# Revit family: КШ РАШВОРК  арт.7025 .rfa
name_source: partatom
category: Арматура трубопроводов
units: mm (PartAtom-declared; Revit-internal decimal feet)

## family parameters
Всегда вертикально = Нет
На основе рабочей плоскости = Нет
Общий = Нет
При загрузке вырезать с полостями = Да
Размер круглого соединителя = Использовать диаметр
Тип детали = Нормальный

## types (11) — shared parameters
ADSK_Единица измерения = шт
ADSK_Завод-изготовитель = ООО "ТД "РАШВОРК"
URL = https://rwru.ru
Изготовитель = ООО "ТД "РАШВОРК"
Корпус = нерж. сталь CF8M
Ручка = нерж. сталь AISI304
Уго_длинна = 115 мм
zero-valued in all types: Отметка по умолчанию

## per-type parameters (varying)
| type | ADSK_Код изделия | ADSK_Масса | DN | DN_соединителя | H | H1 | H11 | H2 | H3 | L | L1 | L2 | L3 | L4 | LL | Lруч | TISO | W | Корпус_ | РАСС | ШISO | Шручки |
| Кран шаровой полнопроходной РАШВОРК 7025 DN008 PN63, CF8M / AISI316 / PTFE, ВР/ВР, ISO 5211, рукоятка-рычаг, кв.9мм | 7025-008-63 | 0.4 | 13 мм | 8 мм | 60 мм | 30 мм | 13 мм | 1 мм | 8 мм | 52 мм | 35 мм | 10 мм | 10 мм | 14 мм | 20 мм | 100 мм | 4 мм | 140 мм | Корпус_ : DN8_10 | 33 мм | 32 мм | 20 мм |
| Кран шаровой полнопроходной РАШВОРК 7025 DN100 PN63, CF8M / AISI316 / PTFE, ВР/ВР, ISO 5211, рукоятка-рычаг, кв.17мм | 7025-100-63 | 14.37 | 94 мм | 100 мм | 182 мм | 131 мм | 76 мм | 8 мм | 15 мм | 213 мм | 152 мм | 33 мм | 27 мм | 29 мм | 115 мм | 245 мм | 10 мм | 320 мм | Корпус_ : DN100 | 152 мм | 102 мм | 32 мм |
| Кран шаровой полнопроходной РАШВОРК 7025 DN010 PN63, CF8M / AISI316 / PTFE, ВР/ВР, ISO 5211, рукоятка-рычаг, кв.9мм | 7025-010-63 | 0.42 | 13 мм | 10 мм | 60 мм | 30 мм | 13 мм | 1 мм | 8 мм | 52 мм | 35 мм | 10 мм | 10 мм | 14 мм | 20 мм | 100 мм | 4 мм | 140 мм | Корпус_ : DN8_10 | 33 мм | 32 мм | 20 мм |
| Кран шаровой полнопроходной РАШВОРК 7025 DN015 PN63, CF8M / AISI316 / PTFE, ВР/ВР, ISO 5211, рукоятка-рычаг, кв.9мм | 7025-015-63 | 0.53 | 15 мм | 15 мм | 68 мм | 37 мм | 16 мм | 1 мм | 10 мм | 62 мм | 38 мм | 10 мм | 10 мм | 16 мм | 25 мм | 100 мм | 5 мм | 140 мм | Корпус_ : DN15 | 38 мм | 42 мм | 20 мм |
| Кран шаровой полнопроходной РАШВОРК 7025 DN020 PN63, CF8M / AISI316 / PTFE, ВР/ВР, ISO 5211, рукоятка-рычаг, кв.9мм | 7025-020-63 | 0.68 | 20 мм | 20 мм | 72 мм | 41 мм | 20 мм | 1 мм | 6 мм | 72 мм | 48 мм | 14 мм | 10 мм | 16 мм | 31 мм | 100 мм | 5 мм | 140 мм | Корпус_ : DN20 | 48 мм | 42 мм | 20 мм |
| Кран шаровой полнопроходной РАШВОРК 7025 DN025 PN63, CF8M / AISI316 / PTFE, ВР/ВР, ISO 5211, рукоятка-рычаг, кв.11мм | 7025-025-63 | 0.97 | 25 мм | 25 мм | 86 мм | 49 мм | 25 мм | 2 мм | 11 мм | 72 мм | 51 мм | 16 мм | 10 мм | 18 мм | 39 мм | 90 мм | 6 мм | 160 мм | Корпус_ : DN25 | 51 мм | 50 мм | 22 мм |
| Кран шаровой полнопроходной РАШВОРК 7025 DN032 PN63, CF8M / AISI316 / PTFE, ВР/ВР, ISO 5211, рукоятка-рычаг, кв.11мм | 7025-032-63 | 1.55 | 32 мм | 32 мм | 94 мм | 53 мм | 30 мм | 2 мм | 11 мм | 72 мм | 55 мм | 15 мм | 10 мм | 18 мм | 48 мм | 90 мм | 6 мм | 160 мм | Корпус_ : DN32 | 64 мм | 50 мм | 22 мм |
| Кран шаровой полнопроходной РАШВОРК 7025 DN040 PN63, CF8M / AISI316 / PTFE, ВР/ВР, ISO 5211, рукоятка-рычаг, кв.14мм | 7025-040-63 | 2.18 | 38 мм | 40 мм | 101 мм | 62 мм | 34 мм | 2 мм | 16 мм | 103 мм | 71 мм | 18 мм | 16 мм | 23 мм | 54 мм | 130 мм | 6 мм | 185 мм | Корпус_ : DN40 | 71 мм | 70 мм | 25 мм |
| Кран шаровой полнопроходной РАШВОРК 7025 DN050 PN63, CF8M / AISI316 / PTFE, ВР/ВР, ISO 5211, рукоятка-рычаг, кв.14мм | 7025-050-63 | 3.19 | 50 мм | 50 мм | 110 мм | 71 мм | 44 мм | 2 мм | 16 мм | 126 мм | 90 мм | 20 мм | 16 мм | 23 мм | 68 мм | 130 мм | 6 мм | 185 мм | Корпус_ : DN50 | 90 мм | 70 мм | 25 мм |
| Кран шаровой полнопроходной РАШВОРК 7025 DN065 PN63, CF8M / AISI316 / PTFE, ВР/ВР, ISO 5211, рукоятка-рычаг, кв.17мм | 7025-065-63 | 6.22 | 65 мм | 65 мм | 143 мм | 96 мм | 55 мм | 2 мм | 16 мм | 158 мм | 112 мм | 25 мм | 20 мм | 30 мм | 85 мм | 155 мм | 10 мм | 230 мм | Корпус_ : DN65 | 112 мм | 102 мм | 25 мм |
| Кран шаровой полнопроходной РАШВОРК 7025 DN080 PN63, CF8M / AISI316 / PTFE, ВР/ВР, ISO 5211, рукоятка-рычаг, кв.17мм | 7025-080-63 | 8.3 | 76 мм | 80 мм | 157 мм | 109 мм | 62 мм | 3 мм | 16 мм | 179 мм | 128 мм | 28 мм | 20 мм | 30 мм | 96 мм | 155 мм | 10 мм | 230 мм | Корпус_ : DN80 | 128 мм | 102 мм | 32 мм |

note: column(s) folded — value = type name in every type: ADSK_Наименование
